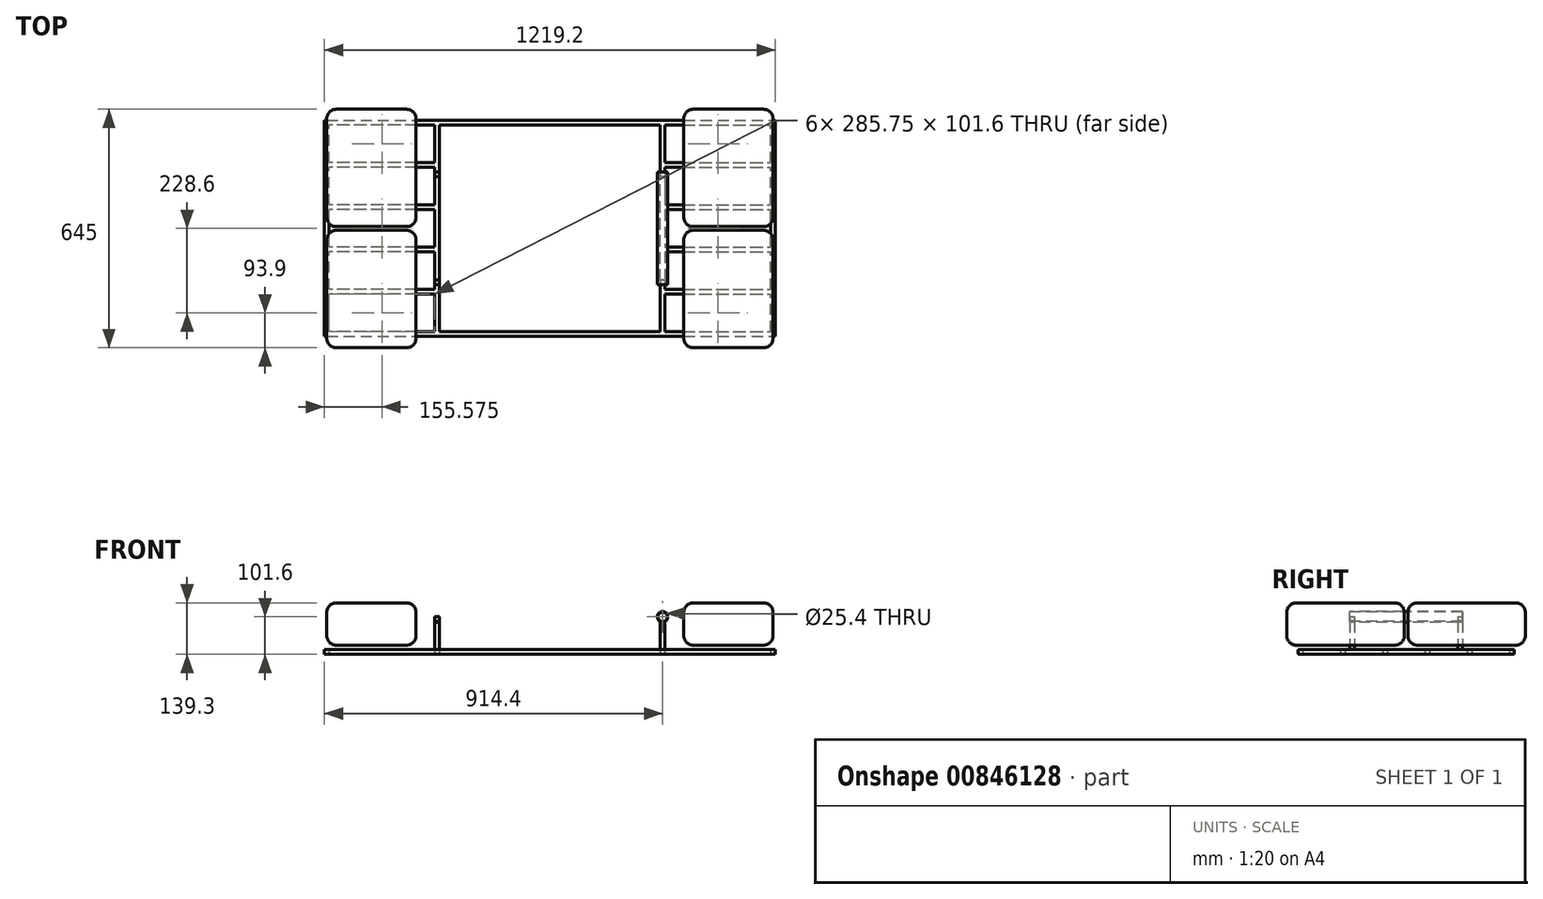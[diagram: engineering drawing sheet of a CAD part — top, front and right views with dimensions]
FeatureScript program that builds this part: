
annotation { "Feature Type Name" : "Feature", "Feature Type Description" : "" }
export const myFeature = defineFeature(function(context is Context, id is Id, definition is map)
    precondition{}
    {
        {
            var Q0;
            Q0=qCreatedBy(makeId("Top.planeOp"),FACE);
            var sketch = newSketch(context, id + "F0", { "sketchPlane" : qUnion([Q0])});
            skLineSegment(sketch, "E0", {"start": v(0, 292.1) * mm, "end": v(-609.6, 292.1) * mm});
            skLineSegment(sketch, "E1", {"start": v(-609.6, 292.1) * mm, "end": v(-609.6, -292.1) * mm});
            skLineSegment(sketch, "E2", {"start": v(-609.6, -292.1) * mm, "end": v(0, -292.1) * mm});
            skLineSegment(sketch, "E3", {"start": v(0, 279.4) * mm, "end": v(-609.6, 279.4) * mm});
            skLineSegment(sketch, "E4", {"start": v(0, -279.4) * mm, "end": v(-609.6, -279.4) * mm});
            skLineSegment(sketch, "E5", {"start": v(-596.9, -279.4) * mm, "end": v(-596.9, 279.4) * mm});
            skLineSegment(sketch, "E6", {"start": v(-311.15, 279.4) * mm, "end": v(-311.15, -279.4) * mm});
            skLineSegment(sketch, "E7", {"start": v(-298.45, -279.4) * mm, "end": v(-298.45, 279.4) * mm});
            skLineSegment(sketch, "E8", {"start": v(-311.15, 177.8) * mm, "end": v(-596.9, 177.8) * mm});
            skLineSegment(sketch, "E9", {"start": v(-311.15, 165.1) * mm, "end": v(-596.9, 165.1) * mm});
            skLineSegment(sketch, "E10", {"start": v(-311.15, 63.5) * mm, "end": v(-596.9, 63.5) * mm});
            skLineSegment(sketch, "E11", {"start": v(-311.15, 50.8) * mm, "end": v(-596.9, 50.8) * mm});
            skLineSegment(sketch, "E12", {"start": v(-311.15, -50.8) * mm, "end": v(-596.9, -50.8) * mm});
            skLineSegment(sketch, "E13", {"start": v(-311.15, -63.5) * mm, "end": v(-596.9, -63.5) * mm});
            skLineSegment(sketch, "E14", {"start": v(-311.15, -165.1) * mm, "end": v(-596.9, -165.1) * mm});
            skLineSegment(sketch, "E15", {"start": v(-311.15, -177.8) * mm, "end": v(-596.9, -177.8) * mm});
            skLineSegment(sketch, "E16", {"start": v(0, 199.95) * mm, "end": v(0, -195.51) * mm, "construction": true});
            skLineSegment(sketch, "E17.MirrorCS", {"start": v(298.45, -279.4) * mm, "end": v(298.45, 279.4) * mm});
            skLineSegment(sketch, "E18.MirrorCS", {"start": v(0, 279.4) * mm, "end": v(609.6, 279.4) * mm});
            skLineSegment(sketch, "E19.MirrorCS", {"start": v(311.15, 63.5) * mm, "end": v(596.9, 63.5) * mm});
            skLineSegment(sketch, "E20.MirrorCS", {"start": v(311.15, 165.1) * mm, "end": v(596.9, 165.1) * mm});
            skLineSegment(sketch, "E21.MirrorCS", {"start": v(0, 292.1) * mm, "end": v(609.6, 292.1) * mm});
            skLineSegment(sketch, "E22.MirrorCS", {"start": v(311.15, 177.8) * mm, "end": v(596.9, 177.8) * mm});
            skLineSegment(sketch, "E23.MirrorCS", {"start": v(311.15, -165.1) * mm, "end": v(596.9, -165.1) * mm});
            skLineSegment(sketch, "E24.MirrorCS", {"start": v(596.9, -279.4) * mm, "end": v(596.9, 279.4) * mm});
            skLineSegment(sketch, "E25.MirrorCS", {"start": v(311.15, -177.8) * mm, "end": v(596.9, -177.8) * mm});
            skLineSegment(sketch, "E26.MirrorCS", {"start": v(311.15, -63.5) * mm, "end": v(596.9, -63.5) * mm});
            skLineSegment(sketch, "E27.MirrorCS", {"start": v(609.6, -292.1) * mm, "end": v(0, -292.1) * mm});
            skLineSegment(sketch, "E28.MirrorCS", {"start": v(0, -279.4) * mm, "end": v(609.6, -279.4) * mm});
            skLineSegment(sketch, "E29.MirrorCS", {"start": v(311.15, 50.8) * mm, "end": v(596.9, 50.8) * mm});
            skLineSegment(sketch, "E30.MirrorCS", {"start": v(311.15, -50.8) * mm, "end": v(596.9, -50.8) * mm});
            skLineSegment(sketch, "E31.MirrorCS", {"start": v(609.6, 292.1) * mm, "end": v(609.6, -292.1) * mm});
            skLineSegment(sketch, "E32.MirrorCS", {"start": v(311.15, 279.4) * mm, "end": v(311.15, -279.4) * mm});
            skSolve(sketch);
        }
        {
            var Q0;
            Q0 = qSketchRegion(id + "F0", true);
            var Q1;
            {var subQ0=sQuery(id+"F0.wireOp",EDGE,"E8");Q1=makeQuery(id+"F0.imprint","IMPRINT",FACE,{"disambiguationData":[TD([[makeQuery(id+"F0.imprint","IMPRINT",EDGE,{"derivedFrom":subQ0}),1.0]])]});}
            var Q2;
            {var subQ0=sQuery(id+"F0.wireOp",EDGE,"E10");Q2=makeQuery(id+"F0.imprint","IMPRINT",FACE,{"disambiguationData":[TD([[makeQuery(id+"F0.imprint","IMPRINT",EDGE,{"derivedFrom":subQ0}),1.0]])]});}
            var Q3;
            {var subQ0=sQuery(id+"F0.wireOp",EDGE,"RP7xIB5S-JgJZ-Xpgd-NU55-WdPinRz1cYuK");Q3=makeQuery(id+"F0.imprint","IMPRINT",FACE,{"disambiguationData":[TD([[makeQuery(id+"F0.imprint","IMPRINT",EDGE,{"derivedFrom":subQ0}),1.0]])]});}
            var Q4;
            {var subQ7=sQuery(id+"F0.wireOp",EDGE,"E7");Q4=makeQuery(id+"F0.imprint","IMPRINT",FACE,{"disambiguationData":[TD([[makeQuery(id+"F0.imprint","IMPRINT",EDGE,{"derivedFrom":subQ7}),1.0]])]});}
            var Q5;
            {var subQ0=sQuery(id+"F0.wireOp",EDGE,"E12");Q5=makeQuery(id+"F0.imprint","IMPRINT",FACE,{"disambiguationData":[TD([[makeQuery(id+"F0.imprint","IMPRINT",EDGE,{"derivedFrom":subQ0}),1.0]])]});}
            var Q6;
            {var subQ0=sQuery(id+"F0.wireOp",EDGE,"E14");Q6=makeQuery(id+"F0.imprint","IMPRINT",FACE,{"disambiguationData":[TD([[makeQuery(id+"F0.imprint","IMPRINT",EDGE,{"derivedFrom":subQ0}),1.0]])]});}
            var Q7;
            {var subQ7=sQuery(id+"F0.wireOp",EDGE,"E17.MirrorCS");Q7=makeQuery(id+"F0.imprint","IMPRINT",FACE,{"disambiguationData":[TD([[makeQuery(id+"F0.imprint","IMPRINT",EDGE,{"derivedFrom":subQ7}),-1.0]])]});}
            var Q8;
            {var subQ0=sQuery(id+"F0.wireOp",EDGE,"E20.MirrorCS");Q8=makeQuery(id+"F0.imprint","IMPRINT",FACE,{"disambiguationData":[TD([[makeQuery(id+"F0.imprint","IMPRINT",EDGE,{"derivedFrom":subQ0}),1.0]])]});}
            var Q9;
            {var subQ0=sQuery(id+"F0.wireOp",EDGE,"E19.MirrorCS");Q9=makeQuery(id+"F0.imprint","IMPRINT",FACE,{"disambiguationData":[TD([[makeQuery(id+"F0.imprint","IMPRINT",EDGE,{"derivedFrom":subQ0}),-1.0]])]});}
            var Q10;
            {var subQ0=sQuery(id+"F0.wireOp",EDGE,"bb576085-0f68-443b-9c05-7b389d3212270.MirrorCS");Q10=makeQuery(id+"F0.imprint","IMPRINT",FACE,{"disambiguationData":[TD([[makeQuery(id+"F0.imprint","IMPRINT",EDGE,{"derivedFrom":subQ0}),-1.0]])]});}
            var Q11;
            {var subQ0=sQuery(id+"F0.wireOp",EDGE,"E26.MirrorCS");Q11=makeQuery(id+"F0.imprint","IMPRINT",FACE,{"disambiguationData":[TD([[makeQuery(id+"F0.imprint","IMPRINT",EDGE,{"derivedFrom":subQ0}),1.0]])]});}
            var Q12;
            {var subQ0=sQuery(id+"F0.wireOp",EDGE,"E23.MirrorCS");Q12=makeQuery(id+"F0.imprint","IMPRINT",FACE,{"disambiguationData":[TD([[makeQuery(id+"F0.imprint","IMPRINT",EDGE,{"derivedFrom":subQ0}),-1.0]])]});}
            extrude(context, id + "F1", {"entities" : qUnion([Q0, Q1, Q2, Q3, Q4, Q5, Q6, Q7, Q8, Q9, Q10, Q11, Q12]), "depth" : 12.7 * mm, "offsetDistance" : 25 * mm});
        }
        {
            var Q0;
            Q0=makeQuery(id+"F1.opExtrude","CAP_FACE",FACE,{"disambiguationData":[OSD([sQuery(id+"F0.wireOp",EDGE,"E0"),sQuery(id+"F0.wireOp",EDGE,"E1"),sQuery(id+"F0.wireOp",EDGE,"E2"),sQuery(id+"F0.wireOp",EDGE,"E3"),sQuery(id+"F0.wireOp",EDGE,"E4"),sQuery(id+"F0.wireOp",EDGE,"E5"),sQuery(id+"F0.wireOp",EDGE,"E6"),sQuery(id+"F0.wireOp",EDGE,"E7"),sQuery(id+"F0.wireOp",EDGE,"E8"),sQuery(id+"F0.wireOp",EDGE,"E9"),sQuery(id+"F0.wireOp",EDGE,"E10"),sQuery(id+"F0.wireOp",EDGE,"E11"),sQuery(id+"F0.wireOp",EDGE,"RP7xIB5S-JgJZ-Xpgd-NU55-WdPinRz1cYuK"),sQuery(id+"F0.wireOp",EDGE,"ZefCPdUL-5prC-wWJY-yU6i-FMz9tpJDSqq4"),sQuery(id+"F0.wireOp",EDGE,"E12"),sQuery(id+"F0.wireOp",EDGE,"E13"),sQuery(id+"F0.wireOp",EDGE,"E14"),sQuery(id+"F0.wireOp",EDGE,"E15"),sQuery(id+"F0.wireOp",EDGE,"bb576085-0f68-443b-9c05-7b389d3212270.MirrorCS"),sQuery(id+"F0.wireOp",EDGE,"E17.MirrorCS"),sQuery(id+"F0.wireOp",EDGE,"E18.MirrorCS"),sQuery(id+"F0.wireOp",EDGE,"E19.MirrorCS"),sQuery(id+"F0.wireOp",EDGE,"E20.MirrorCS"),sQuery(id+"F0.wireOp",EDGE,"E21.MirrorCS"),sQuery(id+"F0.wireOp",EDGE,"bb576085-0f68-443b-9c05-7b389d3212276.MirrorCS"),sQuery(id+"F0.wireOp",EDGE,"E22.MirrorCS"),sQuery(id+"F0.wireOp",EDGE,"E23.MirrorCS"),sQuery(id+"F0.wireOp",EDGE,"E24.MirrorCS"),sQuery(id+"F0.wireOp",EDGE,"E25.MirrorCS"),sQuery(id+"F0.wireOp",EDGE,"E26.MirrorCS"),sQuery(id+"F0.wireOp",EDGE,"E27.MirrorCS"),sQuery(id+"F0.wireOp",EDGE,"E28.MirrorCS"),sQuery(id+"F0.wireOp",EDGE,"E29.MirrorCS"),sQuery(id+"F0.wireOp",EDGE,"E30.MirrorCS"),sQuery(id+"F0.wireOp",EDGE,"E31.MirrorCS"),sQuery(id+"F0.wireOp",EDGE,"E32.MirrorCS")])],"isStart":false});
            var sketch = newSketch(context, id + "F2", { "sketchPlane" : qUnion([Q0])});
            skLineSegment(sketch, "E33.bottom", {"start": v(-298.45, 152.4) * mm, "end": v(-311.15, 152.4) * mm});
            skLineSegment(sketch, "E33.top", {"start": v(-298.45, 139.7) * mm, "end": v(-311.15, 139.7) * mm});
            skLineSegment(sketch, "E33.left", {"start": v(-298.45, 152.4) * mm, "end": v(-298.45, 139.7) * mm});
            skLineSegment(sketch, "E33.right", {"start": v(-311.15, 152.4) * mm, "end": v(-311.15, 139.7) * mm});
            skPoint(sketch, "E33.middle", {"position": v(-304.8, 146.05) * mm});
            skLineSegment(sketch, "E34", {"start": v(56.43, 0) * mm, "end": v(-74.44, 0) * mm, "construction": true});
            skLineSegment(sketch, "E35", {"start": v(-74.44, 0) * mm, "end": v(0, 80.77) * mm, "construction": true});
            skLineSegment(sketch, "E36", {"start": v(0, 80.77) * mm, "end": v(0, -62.77) * mm, "construction": true});
            skLineSegment(sketch, "E37.MirrorCS", {"start": v(-298.45, -139.7) * mm, "end": v(-311.15, -139.7) * mm});
            skLineSegment(sketch, "E38.MirrorCS", {"start": v(-298.45, -152.4) * mm, "end": v(-298.45, -139.7) * mm});
            skPoint(sketch, "E39.MirrorP", {"position": v(-304.8, -146.05) * mm});
            skLineSegment(sketch, "E40.MirrorCS", {"start": v(-298.45, -152.4) * mm, "end": v(-311.15, -152.4) * mm});
            skLineSegment(sketch, "E41.MirrorCS", {"start": v(-311.15, -152.4) * mm, "end": v(-311.15, -139.7) * mm});
            skLineSegment(sketch, "E42.MirrorCS", {"start": v(311.15, -152.4) * mm, "end": v(311.15, -139.7) * mm});
            skLineSegment(sketch, "E43.MirrorCS", {"start": v(311.15, 152.4) * mm, "end": v(311.15, 139.7) * mm});
            skLineSegment(sketch, "E44.MirrorCS", {"start": v(298.45, -139.7) * mm, "end": v(311.15, -139.7) * mm});
            skLineSegment(sketch, "E45.MirrorCS", {"start": v(298.45, 139.7) * mm, "end": v(311.15, 139.7) * mm});
            skLineSegment(sketch, "E46.MirrorCS", {"start": v(298.45, 152.4) * mm, "end": v(311.15, 152.4) * mm});
            skLineSegment(sketch, "E47.MirrorCS", {"start": v(298.45, 152.4) * mm, "end": v(298.45, 139.7) * mm});
            skLineSegment(sketch, "E48.MirrorCS", {"start": v(298.45, -152.4) * mm, "end": v(298.45, -139.7) * mm});
            skLineSegment(sketch, "E49.MirrorCS", {"start": v(298.45, -152.4) * mm, "end": v(311.15, -152.4) * mm});
            skPoint(sketch, "E50.MirrorP", {"position": v(304.8, -146.05) * mm});
            skPoint(sketch, "E51.MirrorP", {"position": v(304.8, 146.05) * mm});
            skSolve(sketch);
        }
        {
            var Q0;
            Q0 = qSketchRegion(id + "F2", true);
            extrude(context, id + "F3", {"entities" : qUnion([Q0]), "operationType" : NewBodyOperationType.ADD, "depth" : 88.9 * mm, "offsetDistance" : 25 * mm});
        }
        {
            var Q0;
            Q0=makeQuery(id+"F3.opExtrude","SWEPT_FACE",FACE,{"disambiguationData":[OSD([sQuery(id+"F2.wireOp",EDGE,"E49.MirrorCS")])]});
            var sketch = newSketch(context, id + "F4", { "sketchPlane" : qUnion([Q0])});
            skCircle(sketch, "E52", {"center": v(304.8, 101.6) * mm, "radius": 14.29 * mm});
            skLineSegment(sketch, "E53", {"start": v(0, 0) * mm, "end": v(0, 107.53) * mm, "construction": true});
            skCircle(sketch, "E54.MirrorC", {"center": v(-304.8, 101.6) * mm, "radius": 14.29 * mm});
            skCircle(sketch, "E55", {"center": v(304.8, 101.6) * mm, "radius": 12.7 * mm});
            skCircle(sketch, "E56.MirrorC", {"center": v(-304.8, 101.6) * mm, "radius": 12.7 * mm});
            skSolve(sketch);
        }
        {
            var Q0;
            {var subQ1=sQuery(id+"F2.wireOp",EDGE,"E49.MirrorCS");var subQ6=makeQuery(id+"F3.opExtrude","CAP_EDGE",EDGE,{"disambiguationData":[OSD([subQ1])],"isStart":false});Q0=makeQuery(id+"F4.imprint","IMPRINT",FACE,{"disambiguationData":[TD([[makeQuery(id+"F4.imprint","IMPRINT",EDGE,{"derivedFrom":subQ6}),-1.0]])]});}
            var Q1;
            Q1=makeQuery(id+"F4.imprint","IMPRINT",FACE,{"disambiguationData":[TD([[makeQuery(id+"F4.imprint","IMPRINT",EDGE,{"derivedFrom":sQuery(id+"F4.wireOp",EDGE,"E56.MirrorC")}),-1.0]])]});
            var Q2;
            Q2=makeQuery(id+"F3.opExtrude","SWEPT_FACE",FACE,{"disambiguationData":[OSD([sQuery(id+"F2.wireOp",EDGE,"E46.MirrorCS")])]});
            extrude(context, id + "F5", {"entities" : qUnion([Q0, Q1]), "operationType" : NewBodyOperationType.REMOVE, "endBound" : BoundingType.UP_TO_SURFACE, "oppositeDirection" : true, "depth" : 25 * mm, "endBoundEntityFace" : qUnion([Q2]), "offsetDistance" : 25 * mm});
        }
        {
            var Q0;
            {var subQ0=sQuery(id+"F4.wireOp",EDGE,"E52");var subQ1=sQuery(id+"F2.wireOp",EDGE,"E49.MirrorCS");var subQ2=makeQuery(id+"F3.opExtrude","SWEPT_EDGE",EDGE,{"disambiguationData":[OSD([sQuery(id+"F0.wireOp",EDGE,"E23.MirrorCS"),sQuery(id+"F2.wireOp",EDGE,"E42.MirrorCS"),subQ1])]});var subQ3=makeQuery(id+"F4.imprint","INTERSECT",VERTEX,{"derivedFrom":[subQ2,subQ0]});Q0=makeQuery(id+"F4.imprint","IMPRINT",FACE,{"disambiguationData":[TD([[makeQuery(id+"F4.imprint","IMPRINT",EDGE,{"disambiguationData":[TD([[subQ3,-1.0]])],"derivedFrom":subQ0}),1.0]])]});}
            var Q1;
            Q1=makeQuery(id+"F4.imprint","IMPRINT",FACE,{"disambiguationData":[TD([[makeQuery(id+"F4.imprint","IMPRINT",EDGE,{"derivedFrom":sQuery(id+"F4.wireOp",EDGE,"E54.MirrorC")}),-1.0]])]});
            var Q2;
            {var subQ0=sQuery(id+"F4.wireOp",EDGE,"E52");var subQ1=sQuery(id+"F2.wireOp",EDGE,"E49.MirrorCS");var subQ2=makeQuery(id+"F3.opExtrude","SWEPT_EDGE",EDGE,{"disambiguationData":[OSD([sQuery(id+"F0.wireOp",EDGE,"E23.MirrorCS"),sQuery(id+"F2.wireOp",EDGE,"E42.MirrorCS"),subQ1])]});var subQ3=makeQuery(id+"F4.imprint","INTERSECT",VERTEX,{"derivedFrom":[subQ2,subQ0]});Q2=makeQuery(id+"F4.imprint","IMPRINT",FACE,{"disambiguationData":[TD([[makeQuery(id+"F4.imprint","IMPRINT",EDGE,{"disambiguationData":[TD([[subQ3,1.0]])],"derivedFrom":subQ0}),1.0]])]});}
            var Q3;
            Q3=makeQuery(id+"F3.opExtrude","SWEPT_FACE",FACE,{"disambiguationData":[OSD([sQuery(id+"F2.wireOp",EDGE,"E33.bottom")])]});
            extrude(context, id + "F6", {"entities" : qUnion([Q0, Q1, Q2]), "operationType" : NewBodyOperationType.ADD, "endBound" : BoundingType.UP_TO_SURFACE, "oppositeDirection" : true, "depth" : 25 * mm, "endBoundEntityFace" : qUnion([Q3]), "offsetDistance" : 25 * mm});
        }
        {
            var Q0;
            Q0=qCreatedBy(makeId("Top.planeOp"),FACE);
            cPlane(context, id + "F7", {"entities" : qUnion([Q0]), "cplaneType" : CPlaneType.OFFSET, "offset" : 25 * mm, "width" : 150 * mm, "height" : 150 * mm});
        }
        {
            var Q0;
            Q0=qCreatedBy(id+"F7.planeOp",FACE);
            var sketch = newSketch(context, id + "F8", { "sketchPlane" : qUnion([Q0])});
            skLineSegment(sketch, "E57.bottom", {"start": v(603.25, 322.5) * mm, "end": v(361.95, 322.5) * mm});
            skLineSegment(sketch, "E57.top", {"start": v(603.25, 5) * mm, "end": v(361.95, 5) * mm});
            skLineSegment(sketch, "E57.left", {"start": v(603.25, 322.5) * mm, "end": v(603.25, 5) * mm});
            skLineSegment(sketch, "E57.right", {"start": v(361.95, 322.5) * mm, "end": v(361.95, 5) * mm});
            skPoint(sketch, "E57.middle", {"position": v(482.6, 163.75) * mm});
            skLineSegment(sketch, "E58", {"start": v(-120.85, 0) * mm, "end": v(0, 0) * mm, "construction": true});
            skLineSegment(sketch, "E59", {"start": v(0, 0) * mm, "end": v(0, 151.2) * mm, "construction": true});
            skLineSegment(sketch, "E60.MirrorCS", {"start": v(603.25, -322.5) * mm, "end": v(361.95, -322.5) * mm});
            skLineSegment(sketch, "E61.MirrorCS", {"start": v(361.95, -322.5) * mm, "end": v(361.95, -5) * mm});
            skLineSegment(sketch, "E62.MirrorCS", {"start": v(603.25, -5) * mm, "end": v(361.95, -5) * mm});
            skLineSegment(sketch, "E63.MirrorCS", {"start": v(603.25, -322.5) * mm, "end": v(603.25, -5) * mm});
            skPoint(sketch, "E64.MirrorP", {"position": v(482.6, -163.75) * mm});
            skLineSegment(sketch, "E65.MirrorCS", {"start": v(-603.25, 5) * mm, "end": v(-361.95, 5) * mm});
            skLineSegment(sketch, "E66.MirrorCS", {"start": v(-361.95, -322.5) * mm, "end": v(-361.95, -5) * mm});
            skPoint(sketch, "E67.MirrorP", {"position": v(-482.6, 163.75) * mm});
            skLineSegment(sketch, "E68.MirrorCS", {"start": v(-603.25, 322.5) * mm, "end": v(-603.25, 5) * mm});
            skPoint(sketch, "E69.MirrorP", {"position": v(-482.6, -163.75) * mm});
            skLineSegment(sketch, "E70.MirrorCS", {"start": v(-603.25, -322.5) * mm, "end": v(-603.25, -5) * mm});
            skLineSegment(sketch, "E71.MirrorCS", {"start": v(-361.95, 322.5) * mm, "end": v(-361.95, 5) * mm});
            skLineSegment(sketch, "E72.MirrorCS", {"start": v(-603.25, -322.5) * mm, "end": v(-361.95, -322.5) * mm});
            skLineSegment(sketch, "E73.MirrorCS", {"start": v(-603.25, 322.5) * mm, "end": v(-361.95, 322.5) * mm});
            skLineSegment(sketch, "E74.MirrorCS", {"start": v(-603.25, -5) * mm, "end": v(-361.95, -5) * mm});
            skSolve(sketch);
        }
        {
            var Q0;
            Q0 = qSketchRegion(id + "F8", true);
            extrude(context, id + "F9", {"entities" : qUnion([Q0]), "depth" : 114.3 * mm, "offsetDistance" : 25 * mm});
        }
        {
            var Q0;
            Q0=makeQuery(id+"F9.opExtrude","CAP_FACE",FACE,{"disambiguationData":[OSD([sQuery(id+"F8.wireOp",EDGE,"E65.MirrorCS"),sQuery(id+"F8.wireOp",EDGE,"E68.MirrorCS"),sQuery(id+"F8.wireOp",EDGE,"E71.MirrorCS"),sQuery(id+"F8.wireOp",EDGE,"E73.MirrorCS")])],"isStart":false});
            var Q1;
            Q1=makeQuery(id+"F9.opExtrude","CAP_FACE",FACE,{"disambiguationData":[OSD([sQuery(id+"F8.wireOp",EDGE,"E66.MirrorCS"),sQuery(id+"F8.wireOp",EDGE,"E70.MirrorCS"),sQuery(id+"F8.wireOp",EDGE,"E72.MirrorCS"),sQuery(id+"F8.wireOp",EDGE,"E74.MirrorCS")])],"isStart":false});
            var Q2;
            Q2=makeQuery(id+"F9.opExtrude","CAP_FACE",FACE,{"disambiguationData":[OSD([sQuery(id+"F8.wireOp",EDGE,"E60.MirrorCS"),sQuery(id+"F8.wireOp",EDGE,"E61.MirrorCS"),sQuery(id+"F8.wireOp",EDGE,"E62.MirrorCS"),sQuery(id+"F8.wireOp",EDGE,"E63.MirrorCS")])],"isStart":false});
            var Q3;
            Q3=makeQuery(id+"F9.opExtrude","CAP_FACE",FACE,{"disambiguationData":[OSD([sQuery(id+"F8.wireOp",EDGE,"E57.bottom"),sQuery(id+"F8.wireOp",EDGE,"E57.top"),sQuery(id+"F8.wireOp",EDGE,"E57.left"),sQuery(id+"F8.wireOp",EDGE,"E57.right")])],"isStart":false});
            var Q4;
            Q4=makeQuery(id+"F9.opExtrude","SWEPT_FACE",FACE,{"disambiguationData":[OSD([sQuery(id+"F8.wireOp",EDGE,"E68.MirrorCS")])]});
            var Q5;
            Q5=makeQuery(id+"F9.opExtrude","SWEPT_FACE",FACE,{"disambiguationData":[OSD([sQuery(id+"F8.wireOp",EDGE,"E70.MirrorCS")])]});
            var Q6;
            Q6=makeQuery(id+"F9.opExtrude","SWEPT_FACE",FACE,{"disambiguationData":[OSD([sQuery(id+"F8.wireOp",EDGE,"E57.right")])]});
            var Q7;
            Q7=makeQuery(id+"F9.opExtrude","SWEPT_FACE",FACE,{"disambiguationData":[OSD([sQuery(id+"F8.wireOp",EDGE,"E61.MirrorCS")])]});
            var Q8;
            Q8=makeQuery(id+"F9.opExtrude","CAP_FACE",FACE,{"disambiguationData":[OSD([sQuery(id+"F8.wireOp",EDGE,"E65.MirrorCS"),sQuery(id+"F8.wireOp",EDGE,"E68.MirrorCS"),sQuery(id+"F8.wireOp",EDGE,"E71.MirrorCS"),sQuery(id+"F8.wireOp",EDGE,"E73.MirrorCS")])],"isStart":true});
            var Q9;
            Q9=makeQuery(id+"F9.opExtrude","CAP_FACE",FACE,{"disambiguationData":[OSD([sQuery(id+"F8.wireOp",EDGE,"E66.MirrorCS"),sQuery(id+"F8.wireOp",EDGE,"E70.MirrorCS"),sQuery(id+"F8.wireOp",EDGE,"E72.MirrorCS"),sQuery(id+"F8.wireOp",EDGE,"E74.MirrorCS")])],"isStart":true});
            var Q10;
            Q10=makeQuery(id+"F9.opExtrude","CAP_FACE",FACE,{"disambiguationData":[OSD([sQuery(id+"F8.wireOp",EDGE,"E60.MirrorCS"),sQuery(id+"F8.wireOp",EDGE,"E61.MirrorCS"),sQuery(id+"F8.wireOp",EDGE,"E62.MirrorCS"),sQuery(id+"F8.wireOp",EDGE,"E63.MirrorCS")])],"isStart":true});
            var Q11;
            Q11=makeQuery(id+"F9.opExtrude","CAP_FACE",FACE,{"disambiguationData":[OSD([sQuery(id+"F8.wireOp",EDGE,"E57.bottom"),sQuery(id+"F8.wireOp",EDGE,"E57.top"),sQuery(id+"F8.wireOp",EDGE,"E57.left"),sQuery(id+"F8.wireOp",EDGE,"E57.right")])],"isStart":true});
            var Q12;
            Q12=makeQuery(id+"F9.opExtrude","SWEPT_FACE",FACE,{"disambiguationData":[OSD([sQuery(id+"F8.wireOp",EDGE,"E71.MirrorCS")])]});
            var Q13;
            Q13=makeQuery(id+"F9.opExtrude","SWEPT_FACE",FACE,{"disambiguationData":[OSD([sQuery(id+"F8.wireOp",EDGE,"E57.left")])]});
            var Q14;
            Q14=makeQuery(id+"F9.opExtrude","SWEPT_FACE",FACE,{"disambiguationData":[OSD([sQuery(id+"F8.wireOp",EDGE,"E63.MirrorCS")])]});
            var Q15;
            Q15=makeQuery(id+"F9.opExtrude","SWEPT_FACE",FACE,{"disambiguationData":[OSD([sQuery(id+"F8.wireOp",EDGE,"E66.MirrorCS")])]});
            fillet(context, id + "F10", {"entities" : qUnion([Q0, Q1, Q2, Q3, Q4, Q5, Q6, Q7, Q8, Q9, Q10, Q11, Q12, Q13, Q14, Q15]), "radius" : 25.4 * mm, "tangentPropagation" : true, "allowEdgeOverflow" : false});
        }
    });
